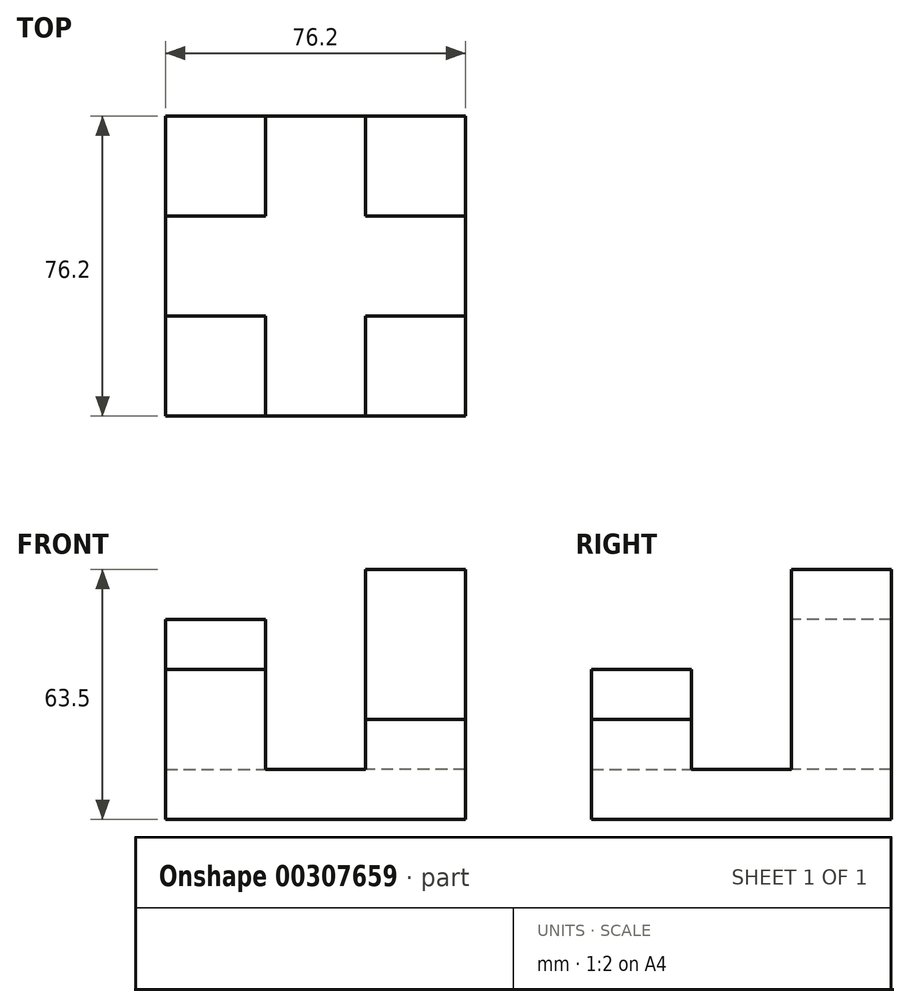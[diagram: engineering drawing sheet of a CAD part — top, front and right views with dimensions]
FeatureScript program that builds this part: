
annotation { "Feature Type Name" : "Feature", "Feature Type Description" : "" }
export const myFeature = defineFeature(function(context is Context, id is Id, definition is map)
    precondition{}
    {
        {
            var Q0;
            Q0=qCreatedBy(makeId("Top.planeOp"),FACE);
            var sketch = newSketch(context, id + "F0", { "sketchPlane" : qUnion([Q0])});
            skLineSegment(sketch, "E0.bottom", {"start": v(-37.57, 37.25) * mm, "end": v(38.63, 37.25) * mm});
            skLineSegment(sketch, "E0.top", {"start": v(-37.57, -38.95) * mm, "end": v(38.63, -38.95) * mm});
            skLineSegment(sketch, "E0.left", {"start": v(-37.57, 37.25) * mm, "end": v(-37.57, -38.95) * mm});
            skLineSegment(sketch, "E0.right", {"start": v(38.63, 37.25) * mm, "end": v(38.63, -38.95) * mm});
            skSolve(sketch);
        }
        {
            var Q0;
            Q0 = qSketchRegion(id + "F0", true);
            extrude(context, id + "F1", {"entities" : qUnion([Q0]), "depth" : -12.7 * mm});
        }
        {
            var Q0;
            Q0=makeQuery(id+"F1.opExtrude","CAP_FACE",FACE,{"disambiguationData":[OSD([sQuery(id+"F0.wireOp",EDGE,"E0.bottom"),sQuery(id+"F0.wireOp",EDGE,"E0.top"),sQuery(id+"F0.wireOp",EDGE,"E0.left"),sQuery(id+"F0.wireOp",EDGE,"E0.right")])],"isStart":true});
            var sketch = newSketch(context, id + "F2", { "sketchPlane" : qUnion([Q0])});
            skLineSegment(sketch, "E1.bottom", {"start": v(38.63, -38.95) * mm, "end": v(13.23, -38.95) * mm});
            skLineSegment(sketch, "E1.top", {"start": v(38.63, -13.55) * mm, "end": v(13.23, -13.55) * mm});
            skLineSegment(sketch, "E1.left", {"start": v(38.63, -38.95) * mm, "end": v(38.63, -13.55) * mm});
            skLineSegment(sketch, "E1.right", {"start": v(13.23, -38.95) * mm, "end": v(13.23, -13.55) * mm});
            skSolve(sketch);
        }
        {
            var Q0;
            Q0 = qSketchRegion(id + "F2", true);
            extrude(context, id + "F3", {"entities" : qUnion([Q0]), "operationType" : NewBodyOperationType.ADD, "depth" : 12.7 * mm});
        }
        {
            var Q0;
            Q0=makeQuery(id+"F1.opExtrude","CAP_FACE",FACE,{"disambiguationData":[OSD([sQuery(id+"F0.wireOp",EDGE,"E0.bottom"),sQuery(id+"F0.wireOp",EDGE,"E0.top"),sQuery(id+"F0.wireOp",EDGE,"E0.left"),sQuery(id+"F0.wireOp",EDGE,"E0.right")])],"isStart":true});
            var sketch = newSketch(context, id + "F4", { "sketchPlane" : qUnion([Q0])});
            skLineSegment(sketch, "E2.bottom", {"start": v(-37.57, -38.95) * mm, "end": v(-12.17, -38.95) * mm});
            skLineSegment(sketch, "E2.top", {"start": v(-37.57, -13.55) * mm, "end": v(-12.17, -13.55) * mm});
            skLineSegment(sketch, "E2.left", {"start": v(-37.57, -38.95) * mm, "end": v(-37.57, -13.55) * mm});
            skLineSegment(sketch, "E2.right", {"start": v(-12.17, -38.95) * mm, "end": v(-12.17, -13.55) * mm});
            skSolve(sketch);
        }
        {
            var Q0;
            Q0=makeQuery(id+"F4.imprint","IMPRINT",FACE,{"disambiguationData":[TD([[makeQuery(id+"F4.imprint","IMPRINT",EDGE,{"derivedFrom":sQuery(id+"F4.wireOp",EDGE,"E2.bottom")}),1.0]])]});
            extrude(context, id + "F5", {"entities" : qUnion([Q0]), "operationType" : NewBodyOperationType.ADD, "depth" : 25.4 * mm});
        }
        {
            var Q0;
            Q0=makeQuery(id+"F1.opExtrude","CAP_FACE",FACE,{"disambiguationData":[OSD([sQuery(id+"F0.wireOp",EDGE,"E0.bottom"),sQuery(id+"F0.wireOp",EDGE,"E0.top"),sQuery(id+"F0.wireOp",EDGE,"E0.left"),sQuery(id+"F0.wireOp",EDGE,"E0.right")])],"isStart":true});
            var sketch = newSketch(context, id + "F6", { "sketchPlane" : qUnion([Q0])});
            skLineSegment(sketch, "E3.bottom", {"start": v(-37.57, 37.25) * mm, "end": v(-12.17, 37.25) * mm});
            skLineSegment(sketch, "E3.top", {"start": v(-37.57, 11.85) * mm, "end": v(-12.17, 11.85) * mm});
            skLineSegment(sketch, "E3.left", {"start": v(-37.57, 37.25) * mm, "end": v(-37.57, 11.85) * mm});
            skLineSegment(sketch, "E3.right", {"start": v(-12.17, 37.25) * mm, "end": v(-12.17, 11.85) * mm});
            skLineSegment(sketch, "E4.bottom", {"start": v(38.63, 37.25) * mm, "end": v(13.23, 37.25) * mm});
            skLineSegment(sketch, "E4.top", {"start": v(38.63, 11.85) * mm, "end": v(13.23, 11.85) * mm});
            skLineSegment(sketch, "E4.left", {"start": v(38.63, 37.25) * mm, "end": v(38.63, 11.85) * mm});
            skLineSegment(sketch, "E4.right", {"start": v(13.23, 37.25) * mm, "end": v(13.23, 11.85) * mm});
            skSolve(sketch);
        }
        {
            var Q0;
            Q0=makeQuery(id+"F6.imprint","IMPRINT",FACE,{"disambiguationData":[TD([[makeQuery(id+"F6.imprint","IMPRINT",EDGE,{"derivedFrom":sQuery(id+"F6.wireOp",EDGE,"E4.bottom")}),-1.0]])]});
            extrude(context, id + "F7", {"entities" : qUnion([Q0]), "operationType" : NewBodyOperationType.ADD, "depth" : 50.8 * mm});
        }
        {
            var Q0;
            Q0=makeQuery(id+"F1.opExtrude","CAP_FACE",FACE,{"disambiguationData":[OSD([sQuery(id+"F0.wireOp",EDGE,"E0.bottom"),sQuery(id+"F0.wireOp",EDGE,"E0.top"),sQuery(id+"F0.wireOp",EDGE,"E0.left"),sQuery(id+"F0.wireOp",EDGE,"E0.right")])],"isStart":true});
            var sketch = newSketch(context, id + "F8", { "sketchPlane" : qUnion([Q0])});
            skLineSegment(sketch, "E5.bottom", {"start": v(-37.57, 37.25) * mm, "end": v(-12.17, 37.25) * mm});
            skLineSegment(sketch, "E5.top", {"start": v(-37.57, 11.85) * mm, "end": v(-12.17, 11.85) * mm});
            skLineSegment(sketch, "E5.left", {"start": v(-37.57, 37.25) * mm, "end": v(-37.57, 11.85) * mm});
            skLineSegment(sketch, "E5.right", {"start": v(-12.17, 37.25) * mm, "end": v(-12.17, 11.85) * mm});
            skSolve(sketch);
        }
        {
            var Q0;
            Q0 = qSketchRegion(id + "F8", true);
            extrude(context, id + "F9", {"entities" : qUnion([Q0]), "operationType" : NewBodyOperationType.ADD, "depth" : 38.1 * mm});
        }
    });
